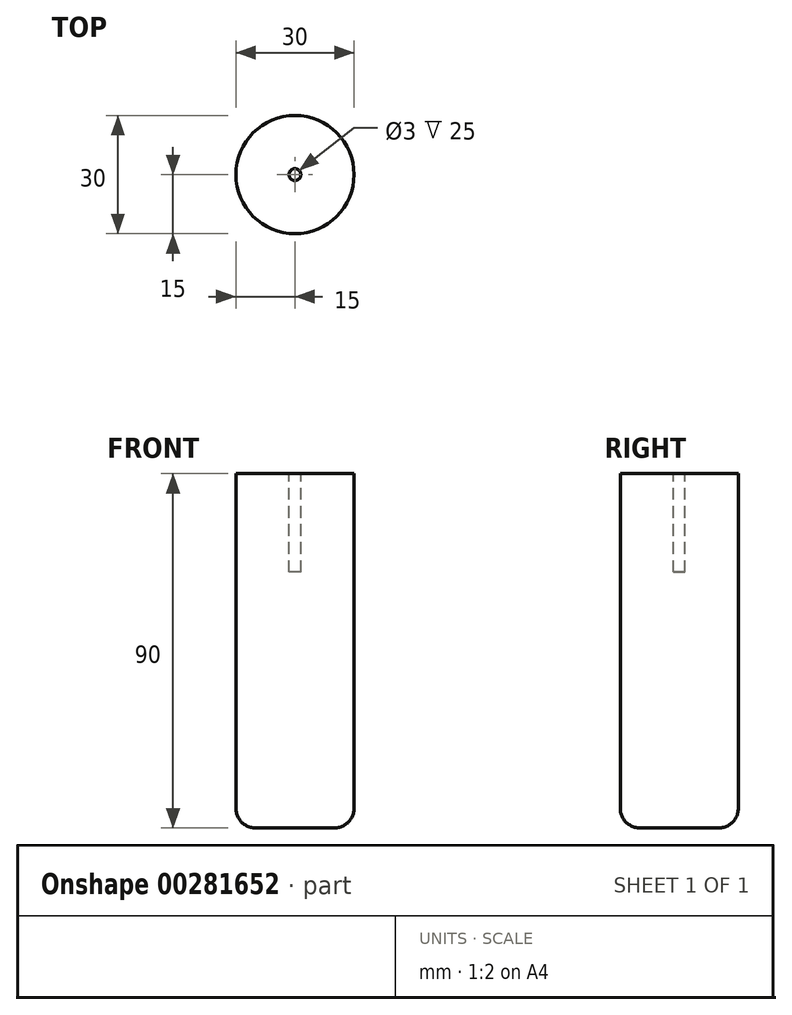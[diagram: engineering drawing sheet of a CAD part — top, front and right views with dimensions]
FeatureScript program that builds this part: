
annotation { "Feature Type Name" : "Feature", "Feature Type Description" : "" }
export const myFeature = defineFeature(function(context is Context, id is Id, definition is map)
    precondition{}
    {
        {
            var Q0;
            Q0=qCreatedBy(makeId("Top.planeOp"),FACE);
            var sketch = newSketch(context, id + "F0", { "sketchPlane" : qUnion([Q0])});
            skCircle(sketch, "E0", {"center": v(0, 0) * mm, "radius": 15 * mm});
            skSolve(sketch);
        }
        {
            var Q0;
            Q0=makeQuery(id+"F0.imprint","IMPRINT",FACE,{"disambiguationData":[TD([[makeQuery(id+"F0.imprint","IMPRINT",EDGE,{"derivedFrom":sQuery(id+"F0.wireOp",EDGE,"E0")}),1.0]])]});
            extrude(context, id + "F1", {"entities" : qUnion([Q0]), "depth" : 90 * mm});
        }
        {
            var Q0;
            Q0=makeQuery(id+"F1.opExtrude","CAP_FACE",FACE,{"disambiguationData":[OSD([sQuery(id+"F0.wireOp",EDGE,"E0")])],"isStart":false});
            var sketch = newSketch(context, id + "F2", { "sketchPlane" : qUnion([Q0])});
            skCircle(sketch, "E1", {"center": v(0, 0) * mm, "radius": 1.5 * mm});
            skSolve(sketch);
        }
        {
            var Q0;
            Q0=makeQuery(id+"F2.imprint","IMPRINT",FACE,{"disambiguationData":[TD([[makeQuery(id+"F2.imprint","IMPRINT",EDGE,{"derivedFrom":sQuery(id+"F2.wireOp",EDGE,"E1")}),1.0]])]});
            extrude(context, id + "F3", {"entities" : qUnion([Q0]), "operationType" : NewBodyOperationType.REMOVE, "oppositeDirection" : true, "depth" : 25 * mm});
        }
        {
            var Q0;
            Q0=makeQuery(id+"F1.opExtrude","CAP_EDGE",EDGE,{"disambiguationData":[OSD([sQuery(id+"F0.wireOp",EDGE,"E0")])],"isStart":true});
            fillet(context, id + "F4", {"entities" : qUnion([Q0]), "radius" : 5 * mm, "tangentPropagation" : true});
        }
    });
